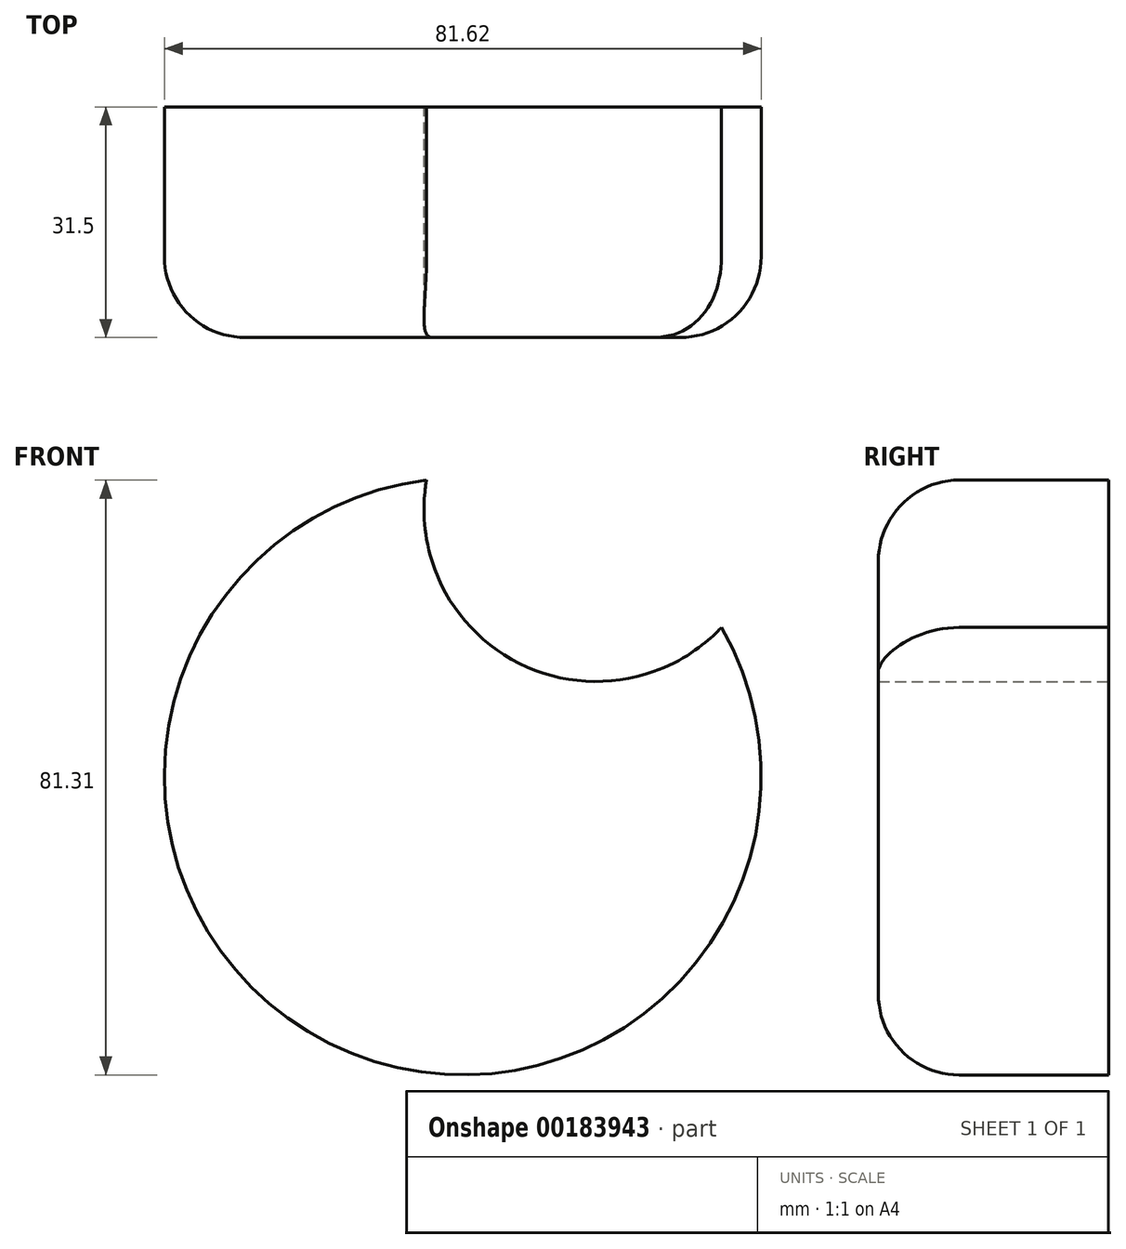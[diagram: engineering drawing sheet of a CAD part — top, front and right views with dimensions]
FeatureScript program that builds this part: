
annotation { "Feature Type Name" : "Feature", "Feature Type Description" : "" }
export const myFeature = defineFeature(function(context is Context, id is Id, definition is map)
    precondition{}
    {
        {
            var Q0;
            Q0=qCreatedBy(makeId("Front.planeOp"),FACE);
            var sketch = newSketch(context, id + "F0", { "sketchPlane" : qUnion([Q0])});
            skArc(sketch, "E0", {"start": v(-4.96, 40.5) * mm, "mid": v(-18.24, -36.5) * mm, "end": v(35.37, 20.36) * mm});
            skArc(sketch, "E1", {"start": v(-4.96, 40.5) * mm, "mid": v(7.72, 15.45) * mm, "end": v(35.37, 20.36) * mm});
            skSolve(sketch);
        }
        {
            var Q0;
            Q0 = qSketchRegion(id + "F0", true);
            extrude(context, id + "F1", {"entities" : qUnion([Q0]), "depth" : 31.5 * mm});
        }
        {
            var Q0;
            Q0=makeQuery(id+"F1.opExtrude","CAP_EDGE",EDGE,{"disambiguationData":[OSD([sQuery(id+"F0.wireOp",EDGE,"E0")])],"isStart":false});
            fillet(context, id + "F2", {"entities" : qUnion([Q0]), "radius" : 11.04 * mm, "tangentPropagation" : true, "allowEdgeOverflow" : false});
        }
        {
            var Q0;
            Q0=qCreatedBy(makeId("Front.planeOp"),FACE);
            cPlane(context, id + "F3", {"entities" : qUnion([Q0]), "cplaneType" : CPlaneType.OFFSET, "offset" : 50.8 * mm, "width" : 152.4 * mm, "height" : 152.4 * mm});
        }
        {
            var Q0;
            Q0=qCreatedBy(id+"F3.planeOp",FACE);
            var sketch = newSketch(context, id + "F4", { "sketchPlane" : qUnion([Q0])});
            skFitSpline(sketch, "E2", {"points": [v(-109.5, -36.46) * mm, v(-132.5, 15.95) * mm, v(-43.67, 23.97) * mm, v(-89.75, 38.92) * mm], "startDerivative": vector(162.28, 143.05) * mm, "endDerivative": vector(-5.9, 68.7) * mm});
            skSolve(sketch);
        }
        {
            var Q0;
            Q0=qCreatedBy(makeId("Front.planeOp"),FACE);
            var sketch = newSketch(context, id + "F5", { "sketchPlane" : qUnion([Q0])});
            skFitSpline(sketch, "E3", {"points": [v(-62.45, 35.83) * mm, v(-69.82, 0) * mm, v(-79.7, -14.73) * mm, v(-106.57, -15.07) * mm], "startDerivative": vector(15.61, -70.14) * mm, "endDerivative": vector(-108.62, 32.6) * mm});
            skSolve(sketch);
        }
        {
            var Q0;
            Q0=sQuery(id+"F5.wireOp",EDGE,"E3");
            var Q1;
            Q1=sQuery(id+"F4.wireOp",EDGE,"E2");
            loft(context, id + "F6", {"bodyType" : ToolBodyType.SURFACE, "wireProfilesArray" : [{ "wireProfileEntities" : qUnion([Q0]) }, { "wireProfileEntities" : qUnion([Q1]) }]});
        }
    });
